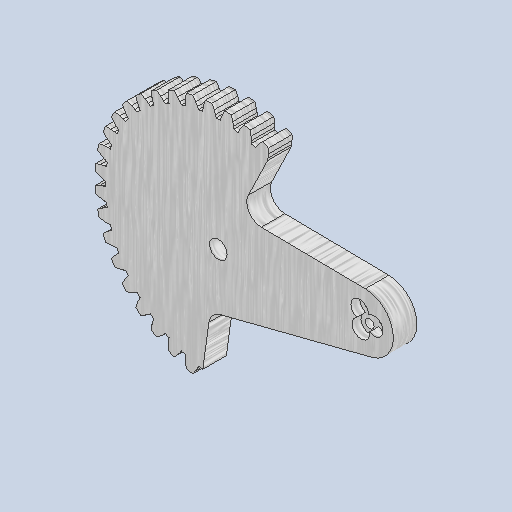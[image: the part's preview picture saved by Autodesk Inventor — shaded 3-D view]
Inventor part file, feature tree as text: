
AUTODESK INVENTOR PART (.ipt)
format: ipt  version: 2023 (Build 270158000, 158)  size: 1,016,832 bytes
history: native  units: mm
features: extrude x4, sketch x4, projected_geometry x1
ambient origin geometry x8: Origin, YZ Plane, XZ Plane, XY Plane, X Axis, Y Axis, Z Axis, Center Point
bodies: Solid1 (feature_tree)
feature tree (9):
  extrude  "Extrusion1"  Depth=8.0mm
  sketch  "Sketch2"  dims[d3=6.13mm d5=7.0mm d49=8.0mm d50=0.0mm d74=5.0mm d79=5.0mm d80=5.0mm d81=15.0mm d82=15.0mm d83=8.0mm d84=0.0mm d85=6.0mm d86=6.0mm d87=6.0mm d88=3.0mm d89=0.0mm d17=0.5mm d18=0.872665mm d19=0.5mm d20=0.872665mm d75=0.872665mm d76=0.5mm d77=0.872665mm]
  extrude  "押し出し6"  Depth=3.0mm
  extrude  "押し出し10"  Depth=8.0mm TaperAngle=0.0deg
  extrude  "押し出し11"  Depth=5.0mm
  sketch  "スケッチ9"
  sketch  "Sketch1"  dims[d0=8.0mm d1=0.0mm d2=6.0mm]
  projected_geometry  "Projected Loop2"
  sketch  "スケッチ7"
